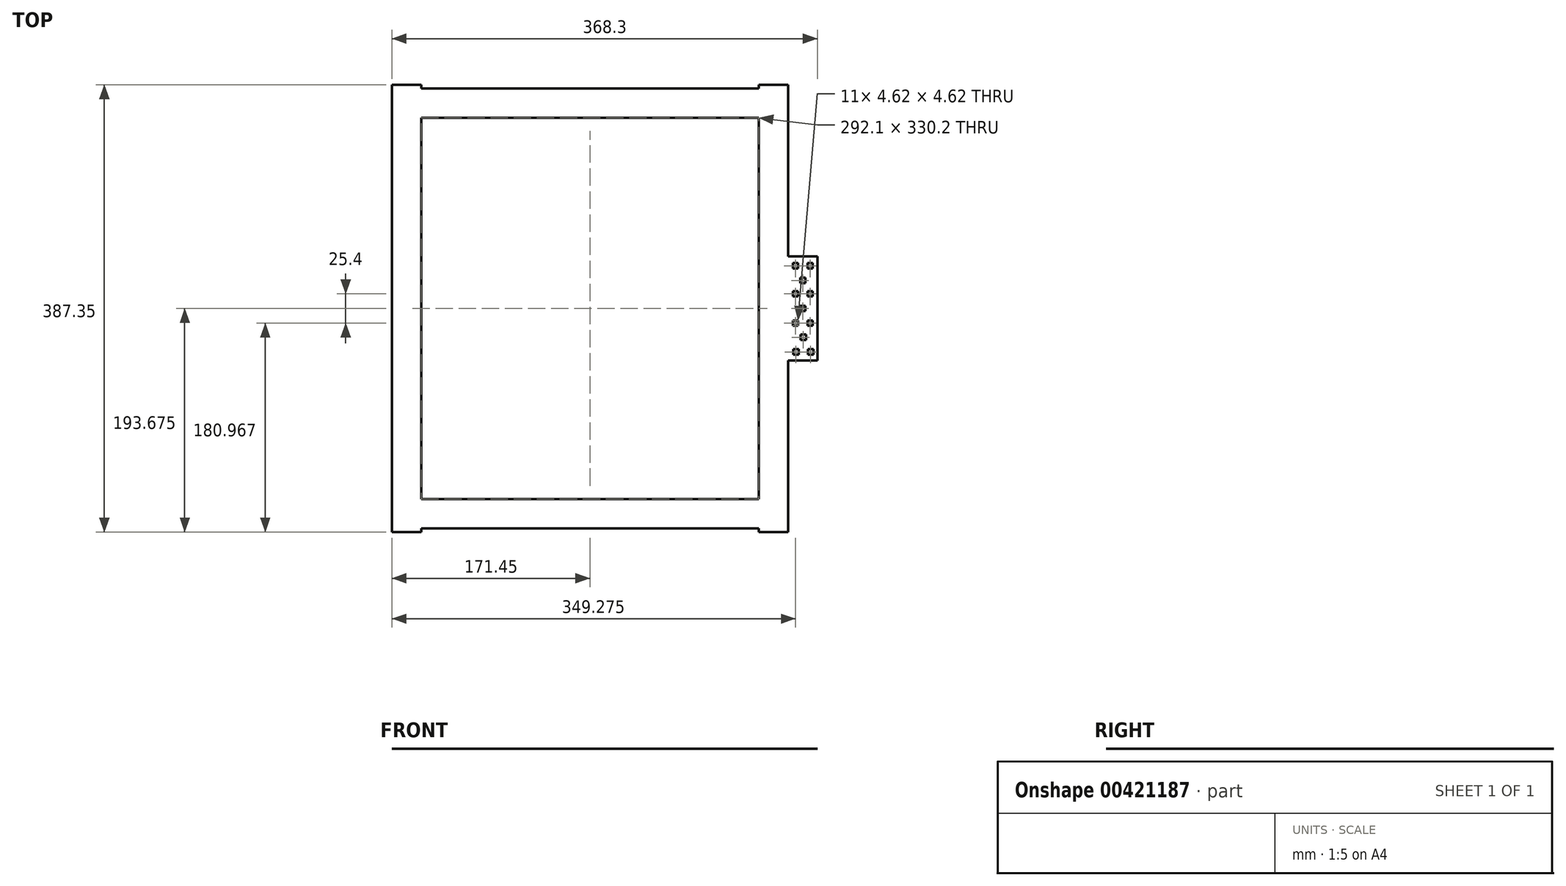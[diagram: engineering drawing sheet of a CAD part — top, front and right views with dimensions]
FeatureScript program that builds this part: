
annotation { "Feature Type Name" : "Feature", "Feature Type Description" : "" }
export const myFeature = defineFeature(function(context is Context, id is Id, definition is map)
    precondition{}
    {
        {
            var Q0;
            Q0=qCreatedBy(makeId("Top.planeOp"),FACE);
            var sketch = newSketch(context, id + "F0", { "sketchPlane" : qUnion([Q0])});
            skLineSegment(sketch, "E0.bottom", {"start": v(215.9, 635.64) * mm, "end": v(508, 635.64) * mm});
            skLineSegment(sketch, "E0.top", {"start": v(215.9, 965.84) * mm, "end": v(508, 965.84) * mm});
            skLineSegment(sketch, "E0.left", {"start": v(215.9, 635.64) * mm, "end": v(215.9, 965.84) * mm});
            skLineSegment(sketch, "E0.right", {"start": v(508, 635.64) * mm, "end": v(508, 965.84) * mm});
            skLineSegment(sketch, "E1", {"start": v(190.5, 635.64) * mm, "end": v(190.5, 610.24) * mm});
            skLineSegment(sketch, "E2.top", {"start": v(190.5, 994.41) * mm, "end": v(215.9, 994.41) * mm});
            skLineSegment(sketch, "E2.left", {"start": v(190.5, 991.24) * mm, "end": v(190.5, 994.41) * mm});
            skLineSegment(sketch, "E2.right", {"start": v(215.9, 991.24) * mm, "end": v(215.9, 994.41) * mm});
            skLineSegment(sketch, "E3.top", {"start": v(190.5, 607.06) * mm, "end": v(215.9, 607.06) * mm});
            skLineSegment(sketch, "E3.left", {"start": v(190.5, 610.24) * mm, "end": v(190.5, 607.06) * mm});
            skLineSegment(sketch, "E3.right", {"start": v(215.9, 610.24) * mm, "end": v(215.9, 607.06) * mm});
            skLineSegment(sketch, "E4.top", {"start": v(533.4, 994.41) * mm, "end": v(508, 994.41) * mm});
            skLineSegment(sketch, "E4.left", {"start": v(533.4, 991.24) * mm, "end": v(533.4, 994.41) * mm});
            skLineSegment(sketch, "E4.right", {"start": v(508, 991.24) * mm, "end": v(508, 994.41) * mm});
            skLineSegment(sketch, "E5.top", {"start": v(533.4, 607.06) * mm, "end": v(508, 607.06) * mm});
            skLineSegment(sketch, "E5.left", {"start": v(533.4, 610.24) * mm, "end": v(533.4, 607.06) * mm});
            skLineSegment(sketch, "E5.right", {"start": v(508, 610.24) * mm, "end": v(508, 607.06) * mm});
            skLineSegment(sketch, "E6", {"start": v(190.5, 607.06) * mm, "end": v(190.5, 755.65) * mm});
            skLineSegment(sketch, "E7", {"start": v(190.5, 857.25) * mm, "end": v(190.5, 994.41) * mm});
            skLineSegment(sketch, "E8", {"start": v(215.9, 610.24) * mm, "end": v(508, 610.24) * mm});
            skLineSegment(sketch, "E9", {"start": v(215.9, 991.24) * mm, "end": v(508, 991.24) * mm});
            skLineSegment(sketch, "E10.1.0.0", {"start": v(554.79, 811.12) * mm, "end": v(550.16, 811.12) * mm});
            skLineSegment(sketch, "E10.1.0.1", {"start": v(550.16, 815.74) * mm, "end": v(550.16, 811.12) * mm});
            skLineSegment(sketch, "E10.1.0.2", {"start": v(537.46, 815.74) * mm, "end": v(537.46, 811.12) * mm});
            skLineSegment(sketch, "E10.1.0.3", {"start": v(543.82, 803.05) * mm, "end": v(543.82, 798.42) * mm});
            skLineSegment(sketch, "E10.1.0.4", {"start": v(542.09, 815.74) * mm, "end": v(542.09, 811.12) * mm});
            skLineSegment(sketch, "E10.1.0.5", {"start": v(537.46, 815.74) * mm, "end": v(542.09, 815.74) * mm});
            skLineSegment(sketch, "E10.1.0.6", {"start": v(537.46, 811.12) * mm, "end": v(542.09, 811.12) * mm});
            skLineSegment(sketch, "E10.1.0.7", {"start": v(548.45, 803.05) * mm, "end": v(548.45, 798.42) * mm});
            skLineSegment(sketch, "E10.1.0.9", {"start": v(548.45, 798.42) * mm, "end": v(543.82, 798.42) * mm});
            skLineSegment(sketch, "E10.1.0.10", {"start": v(554.79, 815.74) * mm, "end": v(550.16, 815.74) * mm});
            skLineSegment(sketch, "E10.1.0.11", {"start": v(554.79, 815.74) * mm, "end": v(554.79, 811.12) * mm});
            skLineSegment(sketch, "E10.2.0.0", {"start": v(554.79, 785.72) * mm, "end": v(550.16, 785.72) * mm});
            skLineSegment(sketch, "E10.2.0.1", {"start": v(550.16, 790.34) * mm, "end": v(550.16, 785.72) * mm});
            skLineSegment(sketch, "E10.2.0.2", {"start": v(537.46, 790.34) * mm, "end": v(537.46, 785.72) * mm});
            skLineSegment(sketch, "E10.2.0.4", {"start": v(542.09, 790.34) * mm, "end": v(542.09, 785.72) * mm});
            skLineSegment(sketch, "E10.2.0.5", {"start": v(537.46, 790.34) * mm, "end": v(542.09, 790.34) * mm});
            skLineSegment(sketch, "E10.2.0.6", {"start": v(537.46, 785.72) * mm, "end": v(542.09, 785.72) * mm});
            skLineSegment(sketch, "E10.2.0.10", {"start": v(554.79, 790.34) * mm, "end": v(550.16, 790.34) * mm});
            skLineSegment(sketch, "E10.2.0.11", {"start": v(554.79, 790.34) * mm, "end": v(554.79, 785.72) * mm});
            skLineSegment(sketch, "E11", {"start": v(548.45, 803.05) * mm, "end": v(543.82, 803.05) * mm});
            skLineSegment(sketch, "E12.1.0.0", {"start": v(554.79, 835.35) * mm, "end": v(550.16, 835.35) * mm});
            skLineSegment(sketch, "E12.1.0.1", {"start": v(550.16, 839.97) * mm, "end": v(550.16, 835.35) * mm});
            skLineSegment(sketch, "E12.1.0.2", {"start": v(537.46, 839.97) * mm, "end": v(537.46, 835.35) * mm});
            skLineSegment(sketch, "E12.1.0.3", {"start": v(543.82, 827.28) * mm, "end": v(543.82, 822.66) * mm});
            skLineSegment(sketch, "E12.1.0.4", {"start": v(542.09, 839.97) * mm, "end": v(542.09, 835.35) * mm});
            skLineSegment(sketch, "E12.1.0.5", {"start": v(537.46, 839.97) * mm, "end": v(542.09, 839.97) * mm});
            skLineSegment(sketch, "E12.1.0.6", {"start": v(537.46, 835.35) * mm, "end": v(542.09, 835.35) * mm});
            skLineSegment(sketch, "E12.1.0.7", {"start": v(548.45, 827.28) * mm, "end": v(548.45, 822.66) * mm});
            skLineSegment(sketch, "E12.1.0.9", {"start": v(548.45, 822.66) * mm, "end": v(543.82, 822.66) * mm});
            skLineSegment(sketch, "E12.1.0.10", {"start": v(554.79, 839.97) * mm, "end": v(550.16, 839.97) * mm});
            skLineSegment(sketch, "E12.1.0.11", {"start": v(554.79, 839.97) * mm, "end": v(554.79, 835.35) * mm});
            skLineSegment(sketch, "E13", {"start": v(548.45, 827.28) * mm, "end": v(543.82, 827.28) * mm});
            skLineSegment(sketch, "E14.1.0.0", {"start": v(537.94, 765.43) * mm, "end": v(542.56, 765.43) * mm});
            skLineSegment(sketch, "E14.1.0.1", {"start": v(542.56, 760.8) * mm, "end": v(542.56, 765.43) * mm});
            skLineSegment(sketch, "E14.1.0.2", {"start": v(555.26, 760.8) * mm, "end": v(555.26, 765.43) * mm});
            skLineSegment(sketch, "E14.1.0.3", {"start": v(548.9, 773.5) * mm, "end": v(548.9, 778.12) * mm});
            skLineSegment(sketch, "E14.1.0.4", {"start": v(550.64, 760.8) * mm, "end": v(550.64, 765.43) * mm});
            skLineSegment(sketch, "E14.1.0.5", {"start": v(555.26, 760.8) * mm, "end": v(550.64, 760.8) * mm});
            skLineSegment(sketch, "E14.1.0.6", {"start": v(555.26, 765.43) * mm, "end": v(550.64, 765.43) * mm});
            skLineSegment(sketch, "E14.1.0.7", {"start": v(544.28, 773.5) * mm, "end": v(544.28, 778.12) * mm});
            skLineSegment(sketch, "E14.1.0.9", {"start": v(544.28, 778.12) * mm, "end": v(548.9, 778.12) * mm});
            skLineSegment(sketch, "E14.1.0.10", {"start": v(537.94, 760.8) * mm, "end": v(542.56, 760.8) * mm});
            skLineSegment(sketch, "E14.1.0.11", {"start": v(537.94, 760.8) * mm, "end": v(537.94, 765.43) * mm});
            skLineSegment(sketch, "E15", {"start": v(544.28, 773.5) * mm, "end": v(548.9, 773.5) * mm});
            skLineSegment(sketch, "E16", {"start": v(558.8, 800.74) * mm, "end": v(558.8, 760.8) * mm});
            skLineSegment(sketch, "E17", {"start": v(558.8, 760.8) * mm, "end": v(558.8, 755.73) * mm});
            skLineSegment(sketch, "E18", {"start": v(558.8, 755.73) * mm, "end": v(533.4, 755.73) * mm});
            skLineSegment(sketch, "E19", {"start": v(558.8, 800.74) * mm, "end": v(558.8, 845.74) * mm});
            skLineSegment(sketch, "E20", {"start": v(558.8, 845.74) * mm, "end": v(533.4, 845.74) * mm});
            skLineSegment(sketch, "E21", {"start": v(533.4, 610.24) * mm, "end": v(533.4, 755.73) * mm});
            skLineSegment(sketch, "E22", {"start": v(533.4, 845.74) * mm, "end": v(533.4, 991.24) * mm});
            skLineSegment(sketch, "E23", {"start": v(190.5, 755.65) * mm, "end": v(190.5, 857.25) * mm});
            skSolve(sketch);
        }
        {
            var Q0;
            Q0=makeQuery(id+"F0.imprint","IMPRINT",FACE,{"disambiguationData":[TD([[makeQuery(id+"F0.imprint","IMPRINT",EDGE,{"derivedFrom":sQuery(id+"F0.wireOp",EDGE,"E0.bottom")}),-1.0]])]});
            extrude(context, id + "F1", {"entities" : qUnion([Q0]), "depth" : 1 / 203.2 * mm});
        }
    });
